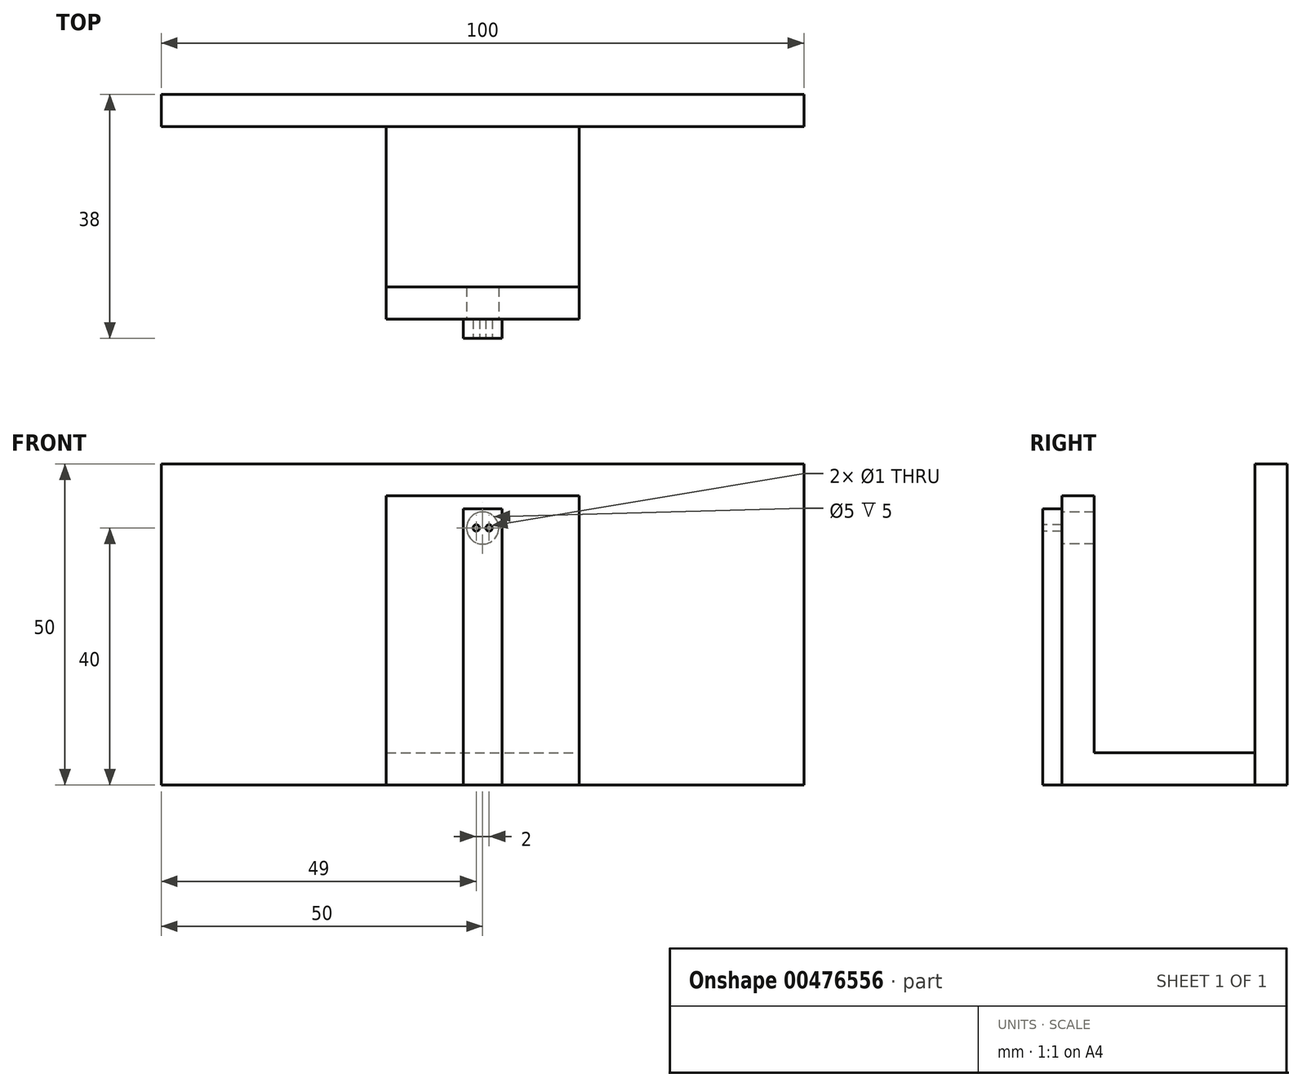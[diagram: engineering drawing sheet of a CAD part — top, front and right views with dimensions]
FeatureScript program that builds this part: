
annotation { "Feature Type Name" : "Feature", "Feature Type Description" : "" }
export const myFeature = defineFeature(function(context is Context, id is Id, definition is map)
    precondition{}
    {
        {
            var Q0;
            Q0=qCreatedBy(makeId("Top.planeOp"),FACE);
            var sketch = newSketch(context, id + "F0", { "sketchPlane" : qUnion([Q0])});
            skLineSegment(sketch, "E0.bottom", {"start": v(15, -15) * mm, "end": v(-15, -15) * mm});
            skLineSegment(sketch, "E0.top", {"start": v(15, 15) * mm, "end": v(-15, 15) * mm});
            skLineSegment(sketch, "E0.left", {"start": v(15, -15) * mm, "end": v(15, 15) * mm});
            skLineSegment(sketch, "E0.right", {"start": v(-15, -15) * mm, "end": v(-15, 15) * mm});
            skPoint(sketch, "E0.middle", {"position": v(0, 0) * mm});
            skSolve(sketch);
        }
        {
            var Q0;
            Q0 = qSketchRegion(id + "F0", true);
            extrude(context, id + "F1", {"entities" : qUnion([Q0]), "depth" : 5 * mm});
        }
        {
            var Q0;
            Q0=makeQuery(id+"F1.opExtrude","CAP_FACE",FACE,{"disambiguationData":[OSD([sQuery(id+"F0.wireOp",EDGE,"E0.bottom"),sQuery(id+"F0.wireOp",EDGE,"E0.top"),sQuery(id+"F0.wireOp",EDGE,"E0.left"),sQuery(id+"F0.wireOp",EDGE,"E0.right")])],"isStart":false});
            var sketch = newSketch(context, id + "F2", { "sketchPlane" : qUnion([Q0])});
            skLineSegment(sketch, "E1.bottom", {"start": v(-15, -15) * mm, "end": v(15, -15) * mm});
            skLineSegment(sketch, "E1.top", {"start": v(-15, -10) * mm, "end": v(15, -10) * mm});
            skLineSegment(sketch, "E1.left", {"start": v(-15, -15) * mm, "end": v(-15, -10) * mm});
            skLineSegment(sketch, "E1.right", {"start": v(15, -15) * mm, "end": v(15, -10) * mm});
            skSolve(sketch);
        }
        {
            var Q0;
            Q0 = qSketchRegion(id + "F2", true);
            extrude(context, id + "F3", {"entities" : qUnion([Q0]), "operationType" : NewBodyOperationType.ADD, "depth" : 40 * mm});
        }
        {
            var Q0;
            Q0=makeQuery(id+"F1.opExtrude","SWEPT_FACE",FACE,{"disambiguationData":[OSD([sQuery(id+"F0.wireOp",EDGE,"E0.top")])]});
            var sketch = newSketch(context, id + "F4", { "sketchPlane" : qUnion([Q0])});
            skLineSegment(sketch, "E2.bottom", {"start": v(50, 0) * mm, "end": v(-50, 0) * mm});
            skLineSegment(sketch, "E2.top", {"start": v(50, 50) * mm, "end": v(-50, 50) * mm});
            skLineSegment(sketch, "E2.left", {"start": v(50, 0) * mm, "end": v(50, 50) * mm});
            skLineSegment(sketch, "E2.right", {"start": v(-50, 0) * mm, "end": v(-50, 50) * mm});
            skSolve(sketch);
        }
        {
            var Q0;
            Q0 = qSketchRegion(id + "F4", true);
            extrude(context, id + "F5", {"entities" : qUnion([Q0]), "operationType" : NewBodyOperationType.ADD, "depth" : 5 * mm});
        }
        {
            var Q0;
            Q0=makeQuery(id+"F3.boolean.opBoolean","MERGE",FACE,{"derivedFrom":[makeQuery(id+"F1.opExtrude","SWEPT_FACE",FACE,{"disambiguationData":[OSD([sQuery(id+"F0.wireOp",EDGE,"E0.bottom")])]}),makeQuery(id+"F3.opExtrude","SWEPT_FACE",FACE,{"disambiguationData":[OSD([sQuery(id+"F2.wireOp",EDGE,"E1.bottom")])]})]});
            var sketch = newSketch(context, id + "F6", { "sketchPlane" : qUnion([Q0])});
            skCircle(sketch, "E3", {"center": v(0, 40) * mm, "radius": 2.5 * mm});
            skSolve(sketch);
        }
        {
            var Q0;
            Q0 = qSketchRegion(id + "F6", true);
            extrude(context, id + "F7", {"entities" : qUnion([Q0]), "operationType" : NewBodyOperationType.REMOVE, "endBound" : BoundingType.UP_TO_NEXT, "oppositeDirection" : true, "depth" : 25 * mm});
        }
        {
            var Q0;
            Q0=makeQuery(id+"F3.boolean.opBoolean","MERGE",FACE,{"derivedFrom":[makeQuery(id+"F1.opExtrude","SWEPT_FACE",FACE,{"disambiguationData":[OSD([sQuery(id+"F0.wireOp",EDGE,"E0.bottom")])]}),makeQuery(id+"F3.opExtrude","SWEPT_FACE",FACE,{"disambiguationData":[OSD([sQuery(id+"F2.wireOp",EDGE,"E1.bottom")])]})]});
            var sketch = newSketch(context, id + "F8", { "sketchPlane" : qUnion([Q0])});
            skLineSegment(sketch, "E4.bottom", {"start": v(3, 0) * mm, "end": v(-3, 0) * mm});
            skLineSegment(sketch, "E4.top", {"start": v(3, 43) * mm, "end": v(-3, 43) * mm});
            skLineSegment(sketch, "E4.left", {"start": v(3, 0) * mm, "end": v(3, 43) * mm});
            skLineSegment(sketch, "E4.right", {"start": v(-3, 0) * mm, "end": v(-3, 43) * mm});
            skSolve(sketch);
        }
        {
            var Q0;
            Q0 = qSketchRegion(id + "F8", true);
            extrude(context, id + "F9", {"entities" : qUnion([Q0]), "operationType" : NewBodyOperationType.ADD, "depth" : 3 * mm});
        }
        {
            var Q0;
            Q0=makeQuery(id+"F9.opExtrude","CAP_FACE",FACE,{"disambiguationData":[OSD([sQuery(id+"F8.wireOp",EDGE,"E4.bottom"),sQuery(id+"F8.wireOp",EDGE,"E4.top"),sQuery(id+"F8.wireOp",EDGE,"E4.left"),sQuery(id+"F8.wireOp",EDGE,"E4.right")])],"isStart":false});
            var sketch = newSketch(context, id + "F10", { "sketchPlane" : qUnion([Q0])});
            skCircle(sketch, "E5", {"center": v(1, 40) * mm, "radius": 0.5 * mm});
            skCircle(sketch, "E6", {"center": v(-1, 40) * mm, "radius": 0.5 * mm});
            skSolve(sketch);
        }
        {
            var Q0;
            Q0 = qSketchRegion(id + "F10", true);
            extrude(context, id + "F11", {"entities" : qUnion([Q0]), "operationType" : NewBodyOperationType.REMOVE, "endBound" : BoundingType.UP_TO_NEXT, "oppositeDirection" : true, "depth" : 25 * mm});
        }
    });
